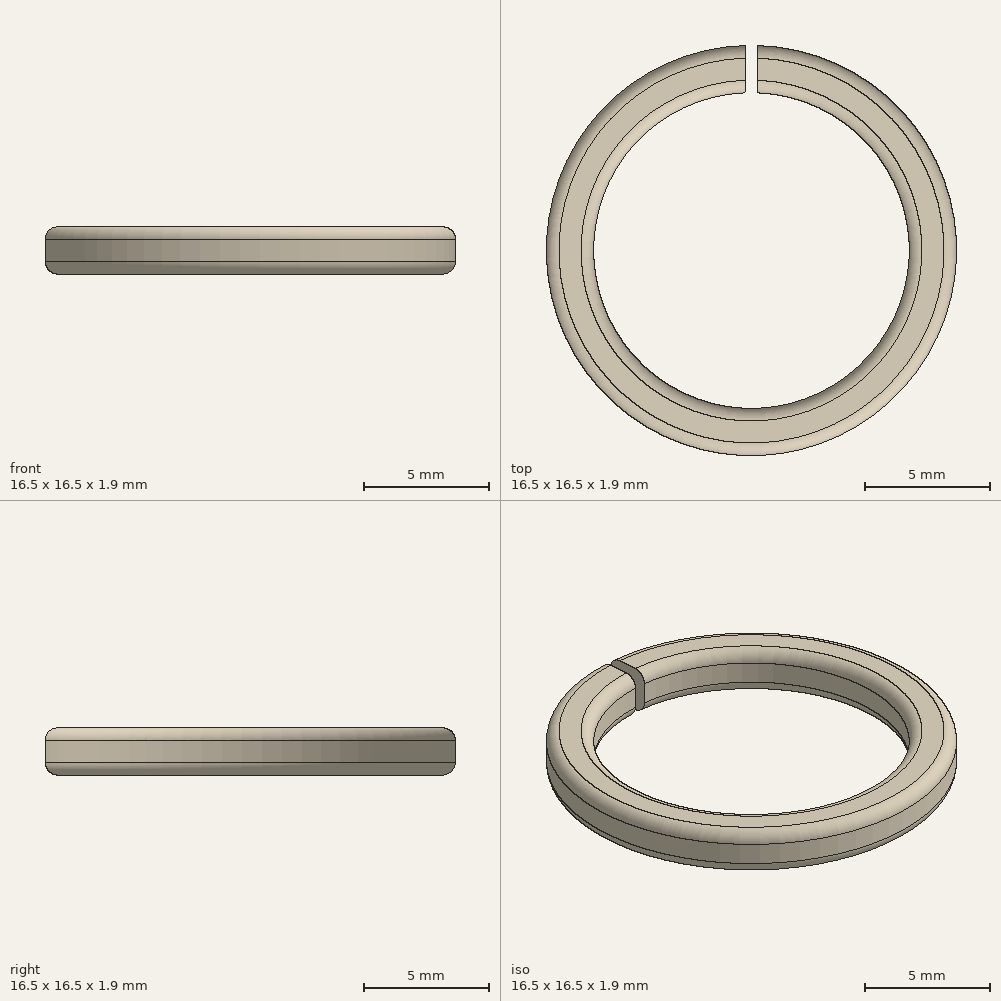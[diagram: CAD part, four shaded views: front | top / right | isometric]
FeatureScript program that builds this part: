
annotation { "Feature Type Name" : "Feature", "Feature Type Description" : "" }
export const myFeature = defineFeature(function(context is Context, id is Id, definition is map)
    precondition{}
    {
        {
            var Q0;
            Q0=qCreatedBy(makeId("Top.planeOp"),FACE);
            var sketch = newSketch(context, id + "F0", { "sketchPlane" : qUnion([Q0])});
            skArc(sketch, "E0", {"start": v(-0.25, 6.34) * mm, "mid": v(0, -6.35) * mm, "end": v(0.25, 6.34) * mm});
            skArc(sketch, "E1.0", {"start": v(-0.25, 8.25) * mm, "mid": v(0, -8.26) * mm, "end": v(0.25, 8.25) * mm});
            skLineSegment(sketch, "E2.0", {"start": v(-0.25, 8.26) * mm, "end": v(-0.25, 6.34) * mm});
            skLineSegment(sketch, "E3.0", {"start": v(0.25, 8.25) * mm, "end": v(0.25, 6.34) * mm});
            skLineSegment(sketch, "E4.trimOffspring", {"start": v(-0.25, -6.34) * mm, "end": v(-0.25, -6.35) * mm});
            skLineSegment(sketch, "E5.trimOffspring", {"start": v(0.25, -6.34) * mm, "end": v(0.25, -6.35) * mm});
            skPoint(sketch, "E6.start.orphan", {"position": v(0, 8.26) * mm});
            skSolve(sketch);
        }
        {
            var Q0;
            {var subQ0=sQuery(id+"F0.wireOp",EDGE,"E1.0");Q0=makeQuery(id+"F0.imprint","IMPRINT",FACE,{"disambiguationData":[TD([[makeQuery(id+"F0.imprint","IMPRINT",EDGE,{"derivedFrom":subQ0}),1.0]])]});}
            extrude(context, id + "F1", {"entities" : qUnion([Q0]), "depth" : 1.9 * mm});
        }
        {
            var Q0;
            Q0=makeQuery(id+"F1.opExtrude","CAP_EDGE",EDGE,{"disambiguationData":[OSD([sQuery(id+"F0.wireOp",EDGE,"E1.0")])],"isStart":false});
            var Q1;
            Q1=makeQuery(id+"F1.opExtrude","CAP_EDGE",EDGE,{"disambiguationData":[OSD([sQuery(id+"F0.wireOp",EDGE,"E0")])],"isStart":true});
            var Q2;
            Q2=makeQuery(id+"F1.opExtrude","CAP_EDGE",EDGE,{"disambiguationData":[OSD([sQuery(id+"F0.wireOp",EDGE,"E0")])],"isStart":false});
            var Q3;
            Q3=makeQuery(id+"F1.opExtrude","CAP_EDGE",EDGE,{"disambiguationData":[OSD([sQuery(id+"F0.wireOp",EDGE,"E1.0")])],"isStart":true});
            fillet(context, id + "F2", {"entities" : qUnion([Q0, Q1, Q2, Q3]), "radius" : 0.5 * mm, "tangentPropagation" : true, "allowEdgeOverflow" : false});
        }
    });
